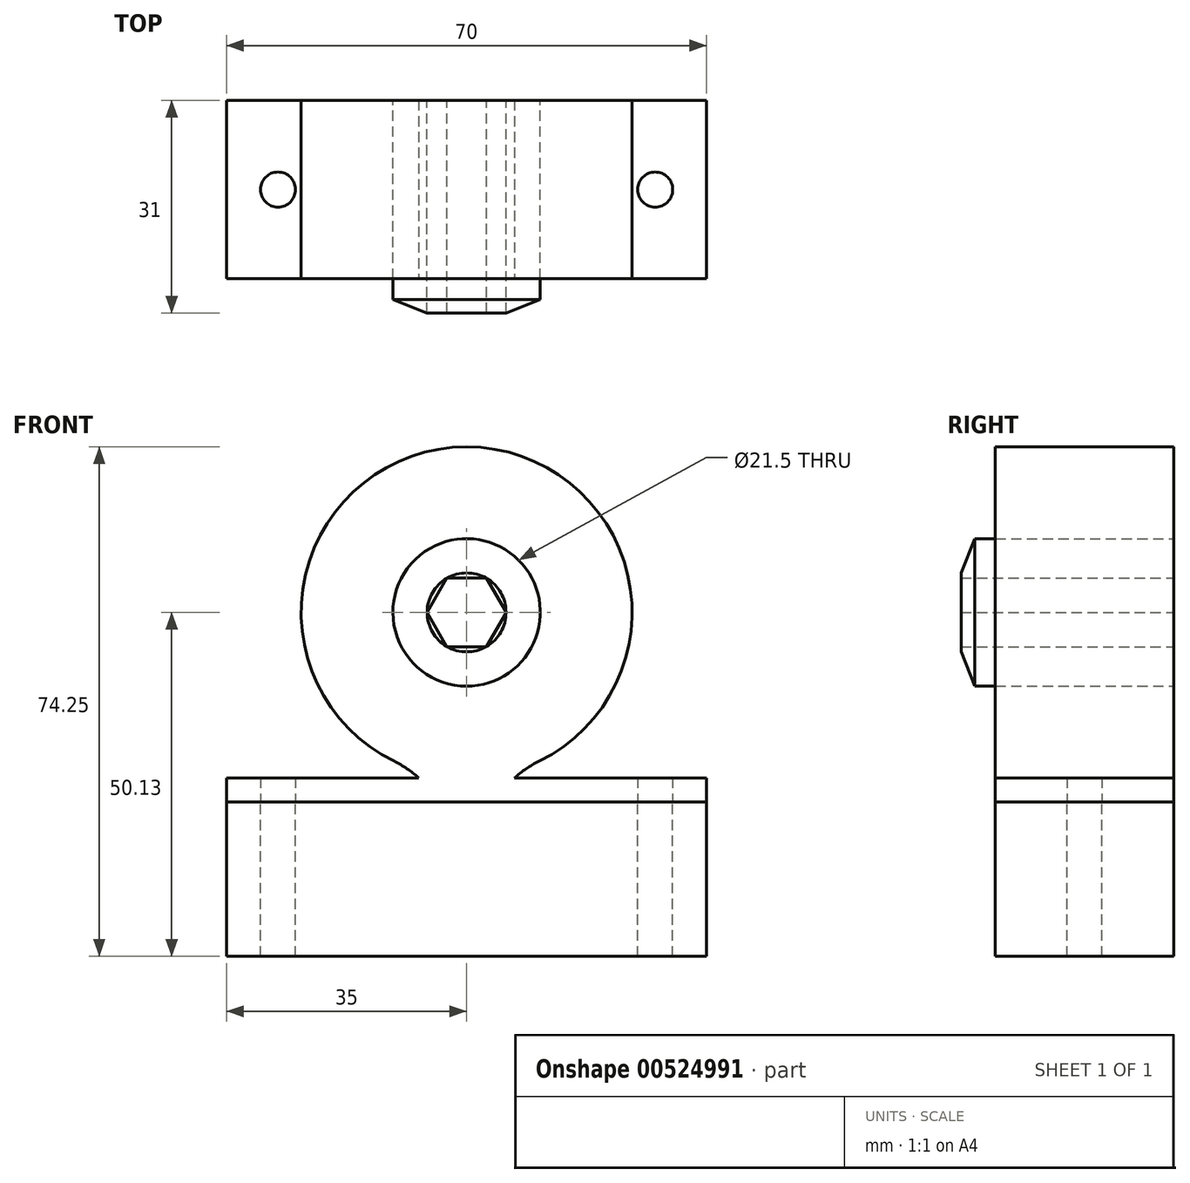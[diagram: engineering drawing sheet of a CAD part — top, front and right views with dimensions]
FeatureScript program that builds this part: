
annotation { "Feature Type Name" : "Feature", "Feature Type Description" : "" }
export const myFeature = defineFeature(function(context is Context, id is Id, definition is map)
    precondition{}
    {
        {
            var Q0;
            Q0=qCreatedBy(makeId("Front.planeOp"),FACE);
            var sketch = newSketch(context, id + "F0", { "sketchPlane" : qUnion([Q0])});
            skCircle(sketch, "E0", {"center": v(0, 0) * mm, "radius": 24.12 * mm});
            skCircle(sketch, "E1", {"center": v(0, 0) * mm, "radius": 10.75 * mm});
            skCircle(sketch, "E2.cCircle", {"center": v(0, 0) * mm, "radius": 5 * mm, "construction": true});
            skLineSegment(sketch, "E2.0", {"start": v(-2.89, 5) * mm, "end": v(2.89, 5) * mm});
            skLineSegment(sketch, "E2.1", {"start": v(2.89, 5) * mm, "end": v(5.77, 0) * mm});
            skLineSegment(sketch, "E2.2", {"start": v(5.77, 0) * mm, "end": v(2.89, -5) * mm});
            skLineSegment(sketch, "E2.3", {"start": v(2.89, -5) * mm, "end": v(-2.89, -5) * mm});
            skLineSegment(sketch, "E2.4", {"start": v(-2.89, -5) * mm, "end": v(-5.77, 0) * mm});
            skLineSegment(sketch, "E2.5", {"start": v(-5.77, 0) * mm, "end": v(-2.89, 5) * mm});
            skPoint(sketch, "E2.0.midPoint", {"position": v(0, 5) * mm});
            skLineSegment(sketch, "E3.bottom", {"start": v(-35, -24.12) * mm, "end": v(35, -24.12) * mm});
            skLineSegment(sketch, "E3.top", {"start": v(-35, -27.63) * mm, "end": v(35, -27.63) * mm});
            skLineSegment(sketch, "E3.left", {"start": v(-35, -24.12) * mm, "end": v(-35, -27.62) * mm});
            skLineSegment(sketch, "E3.right", {"start": v(35, -24.12) * mm, "end": v(35, -27.62) * mm});
            skPoint(sketch, "E4", {"position": v(0, -27.63) * mm});
            skSolve(sketch);
        }
        {
            var Q0;
            Q0=makeQuery(id+"F0.imprint","IMPRINT",FACE,{"disambiguationData":[TD([[makeQuery(id+"F0.imprint","IMPRINT",EDGE,{"derivedFrom":sQuery(id+"F0.wireOp",EDGE,"E0")}),1.0]])]});
            var Q1;
            Q1=makeQuery(id+"F0.imprint","IMPRINT",FACE,{"disambiguationData":[TD([[makeQuery(id+"F0.imprint","IMPRINT",EDGE,{"derivedFrom":sQuery(id+"F0.wireOp",EDGE,"E3.top")}),1.0]])]});
            extrude(context, id + "F1", {"entities" : qUnion([Q0, Q1]), "depth" : 26 * mm, "offsetDistance" : 25 * mm});
        }
        {
            var Q0;
            Q0=makeQuery(id+"F1.opExtrude","SWEPT_FACE",FACE,{"disambiguationData":[OSD([sQuery(id+"F0.wireOp",EDGE,"E3.bottom")])]});
            var sketch = newSketch(context, id + "F2", { "sketchPlane" : qUnion([Q0])});
            skLineSegment(sketch, "E5.bottom", {"start": v(-7, 0) * mm, "end": v(7, 0) * mm});
            skLineSegment(sketch, "E5.top", {"start": v(-7, -26) * mm, "end": v(7, -26) * mm});
            skLineSegment(sketch, "E5.left", {"start": v(-7, 0) * mm, "end": v(-7, -26) * mm});
            skLineSegment(sketch, "E5.right", {"start": v(7, 0) * mm, "end": v(7, -26) * mm});
            skPoint(sketch, "E6", {"position": v(-27.5, -13) * mm});
            skPoint(sketch, "E6.positionSnap0", {"position": v(-35, -13) * mm});
            skPoint(sketch, "E7", {"position": v(27.5, -13) * mm});
            skPoint(sketch, "E7.positionSnap0", {"position": v(35, -13) * mm});
            skSolve(sketch);
        }
        {
            var Q0;
            Q0=makeQuery(id+"F2.imprint","IMPRINT",FACE,{"disambiguationData":[TD([[makeQuery(id+"F2.imprint","IMPRINT",EDGE,{"derivedFrom":sQuery(id+"F2.wireOp",EDGE,"E5.bottom")}),-1.0]])]});
            var Q1;
            Q1=makeQuery(id+"F1.opExtrude","SWEPT_FACE",FACE,{"disambiguationData":[OSD([sQuery(id+"F0.wireOp",EDGE,"E0")])]});
            var Q2;
            Q2=makeQuery(id+"F1.opExtrude","SWEPT_BODY",BODY,{"disambiguationData":[OSD([sQuery(id+"F0.wireOp",EDGE,"E0"),sQuery(id+"F0.wireOp",EDGE,"E1")])]});
            extrude(context, id + "F3", {"entities" : qUnion([Q0]), "operationType" : NewBodyOperationType.ADD, "depth" : 2 * mm, "endBoundEntityFace" : qUnion([Q1]), "endBoundEntityBody" : qUnion([Q2]), "offsetDistance" : 25 * mm});
        }
        {
            var Q0;
            Q0=makeQuery(id+"F3.opExtrude","CAP_EDGE",EDGE,{"disambiguationData":[OSD([sQuery(id+"F2.wireOp",EDGE,"E5.left")])],"isStart":true});
            var Q1;
            Q1=makeQuery(id+"F3.opExtrude","CAP_EDGE",EDGE,{"disambiguationData":[OSD([sQuery(id+"F2.wireOp",EDGE,"E5.right")])],"isStart":true});
            var Q2;
            Q2=makeQuery(id+"F3.boolean.opBoolean","INTERSECT",EDGE,{"derivedFrom":[makeQuery(id+"F1.opExtrude","SWEPT_FACE",FACE,{"disambiguationData":[OSD([sQuery(id+"F0.wireOp",EDGE,"E0")])]}),makeQuery(id+"F3.opExtrude","SWEPT_FACE",FACE,{"disambiguationData":[OSD([sQuery(id+"F2.wireOp",EDGE,"E5.right")])]})]});
            var Q3;
            Q3=makeQuery(id+"F3.boolean.opBoolean","INTERSECT",EDGE,{"derivedFrom":[makeQuery(id+"F1.opExtrude","SWEPT_FACE",FACE,{"disambiguationData":[OSD([sQuery(id+"F0.wireOp",EDGE,"E0")])]}),makeQuery(id+"F3.opExtrude","SWEPT_FACE",FACE,{"disambiguationData":[OSD([sQuery(id+"F2.wireOp",EDGE,"E5.left")])]})]});
            fillet(context, id + "F4", {"entities" : qUnion([Q0, Q1, Q2, Q3]), "radius" : 15 * mm, "tangentPropagation" : true, "allowEdgeOverflow" : false});
        }
        {
            var Q0;
            Q0=makeQuery(id+"F0.imprint","IMPRINT",FACE,{"disambiguationData":[TD([[makeQuery(id+"F0.imprint","IMPRINT",EDGE,{"derivedFrom":sQuery(id+"F0.wireOp",EDGE,"E1")}),1.0]])]});
            extrude(context, id + "F5", {"entities" : qUnion([Q0]), "depth" : 31 * mm, "offsetDistance" : 25 * mm});
        }
        {
            var Q0;
            Q0=makeQuery(id+"F5.opExtrude","CAP_EDGE",EDGE,{"disambiguationData":[OSD([sQuery(id+"F0.wireOp",EDGE,"E1")])],"isStart":false});
            chamfer(context, id + "F6", {"entities" : qUnion([Q0]), "chamferType" : ChamferType.TWO_OFFSETS, "width1" : 2 * mm, "oppositeDirection" : false, "width2" : 5 * mm, "tangentPropagation" : true});
        }
        {
            var Q0;
            Q0=sQuery(id+"F2.wireOp",VERTEX,"E6");
            var Q1;
            Q1=sQuery(id+"F2.wireOp",VERTEX,"E7");
            var Q2;
            Q2=makeQuery(id+"F1.opExtrude","SWEPT_BODY",BODY,{"disambiguationData":[OSD([sQuery(id+"F0.wireOp",EDGE,"E0"),sQuery(id+"F0.wireOp",EDGE,"E1")])]});
            hole(context, id + "F7", {"style" : HoleStyle.SIMPLE, "endStyle" : HoleEndStyle.THROUGH, "standardTappedOrClearance" : lookupTablePath({ "standard" : "ANSI", "fit" : "Normal (ASME)", "size" : "#10", "type" : "Clearance" }), "standardBlindInLast" : lookupTablePath({ "fit" : "Free", "standard" : "ANSI", "size" : "#10", "type" : "Clearance" }), "holeDiameter" : 5.1 * mm, "tappedDepth" : 12 * mm, "tapClearance" : 3, "locations" : qUnion([Q0, Q1]), "scope" : qUnion([Q2]), "startStyle" : HoleStartStyle.SKETCH});
        }
        {
            var Q0;
            Q0=makeQuery(id+"F1.opExtrude","SWEPT_FACE",FACE,{"disambiguationData":[OSD([sQuery(id+"F0.wireOp",EDGE,"E3.top")])]});
            extrude(context, id + "F8", {"entities" : qUnion([Q0]), "depth" : 22.5 * mm, "offsetDistance" : 25 * mm});
        }
    });
